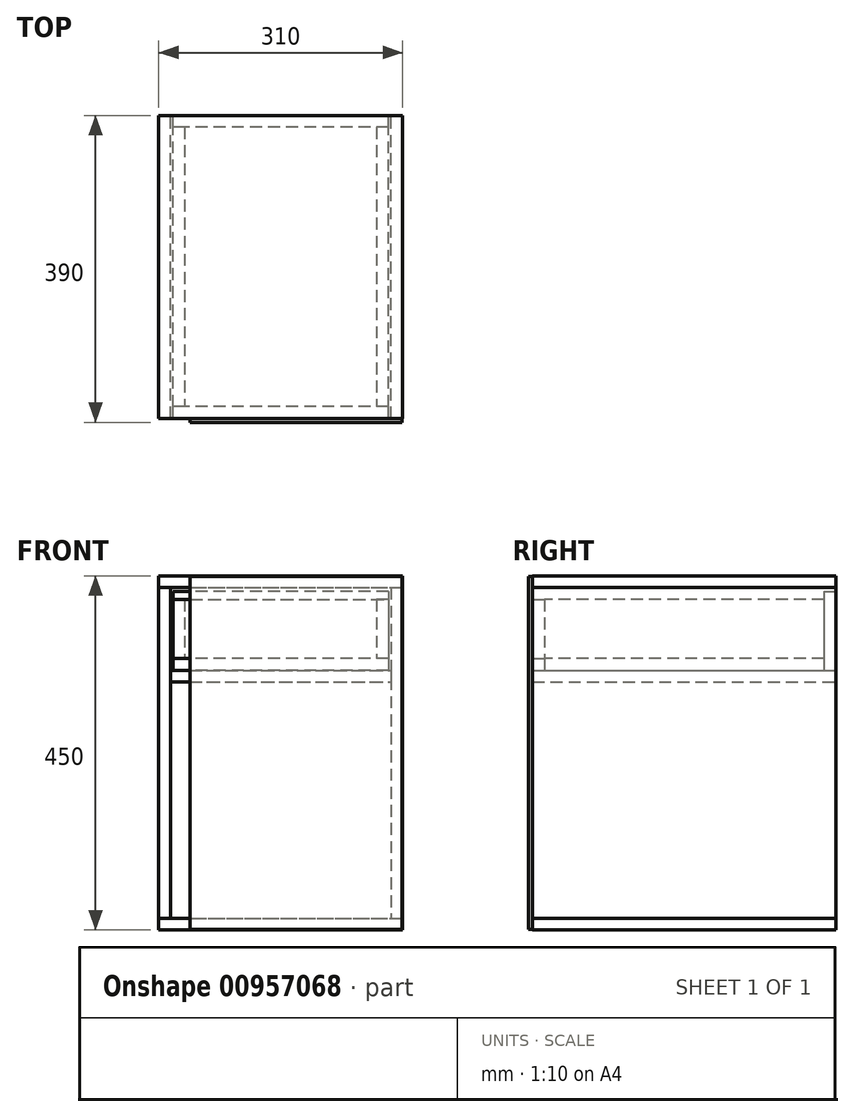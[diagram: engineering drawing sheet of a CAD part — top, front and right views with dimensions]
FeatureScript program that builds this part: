
annotation { "Feature Type Name" : "Feature", "Feature Type Description" : "" }
export const myFeature = defineFeature(function(context is Context, id is Id, definition is map)
    precondition{}
    {
        {
            var Q0;
            Q0=qCreatedBy(makeId("Top.planeOp"),FACE);
            var sketch = newSketch(context, id + "F0", { "sketchPlane" : qUnion([Q0])});
            skLineSegment(sketch, "E0.bottom", {"start": v(0, 0) * mm, "end": v(310, 0) * mm});
            skLineSegment(sketch, "E0.top", {"start": v(0, 385) * mm, "end": v(310, 385) * mm});
            skLineSegment(sketch, "E0.left", {"start": v(0, 0) * mm, "end": v(0, 385) * mm});
            skLineSegment(sketch, "E0.right", {"start": v(310, 0) * mm, "end": v(310, 385) * mm});
            skSolve(sketch);
        }
        {
            var Q0;
            Q0 = qSketchRegion(id + "F0", true);
            extrude(context, id + "F1", {"entities" : qUnion([Q0]), "depth" : 15 * mm, "offsetDistance" : 25 * mm});
        }
        {
            var Q0;
            Q0=makeQuery(id+"F1.opExtrude","CAP_FACE",FACE,{"disambiguationData":[OSD([sQuery(id+"F0.wireOp",EDGE,"E0.bottom"),sQuery(id+"F0.wireOp",EDGE,"E0.top"),sQuery(id+"F0.wireOp",EDGE,"E0.left"),sQuery(id+"F0.wireOp",EDGE,"E0.right")])],"isStart":false});
            var sketch = newSketch(context, id + "F2", { "sketchPlane" : qUnion([Q0])});
            skLineSegment(sketch, "E1.bottom", {"start": v(0, 0) * mm, "end": v(15, 0) * mm});
            skLineSegment(sketch, "E1.top", {"start": v(0, 385) * mm, "end": v(15, 385) * mm});
            skLineSegment(sketch, "E1.left", {"start": v(0, 0) * mm, "end": v(0, 385) * mm});
            skLineSegment(sketch, "E1.right", {"start": v(15, 0) * mm, "end": v(15, 385) * mm});
            skLineSegment(sketch, "E2.bottom", {"start": v(310, 0) * mm, "end": v(295, 0) * mm});
            skLineSegment(sketch, "E2.top", {"start": v(310, 385) * mm, "end": v(295, 385) * mm});
            skLineSegment(sketch, "E2.left", {"start": v(310, 0) * mm, "end": v(310, 385) * mm});
            skLineSegment(sketch, "E2.right", {"start": v(295, 0) * mm, "end": v(295, 385) * mm});
            skSolve(sketch);
        }
        {
            var Q0;
            Q0 = qSketchRegion(id + "F2", true);
            extrude(context, id + "F3", {"entities" : qUnion([Q0]), "depth" : (300 + 15 + 100 + 5) * mm, "offsetDistance" : 25 * mm});
        }
        {
            var Q0;
            Q0=makeQuery(id+"F1.opExtrude","CAP_FACE",FACE,{"disambiguationData":[OSD([sQuery(id+"F0.wireOp",EDGE,"E0.bottom"),sQuery(id+"F0.wireOp",EDGE,"E0.top"),sQuery(id+"F0.wireOp",EDGE,"E0.left"),sQuery(id+"F0.wireOp",EDGE,"E0.right")])],"isStart":false});
            cPlane(context, id + "F4", {"entities" : qUnion([Q0]), "cplaneType" : CPlaneType.OFFSET, "offset" : 300 * mm, "width" : 150 * mm, "height" : 150 * mm});
        }
        {
            var Q0;
            Q0=qCreatedBy(id+"F4.planeOp",FACE);
            var sketch = newSketch(context, id + "F5", { "sketchPlane" : qUnion([Q0])});
            skLineSegment(sketch, "E3.bottom", {"start": v(15, 0) * mm, "end": v(295, 0) * mm});
            skLineSegment(sketch, "E3.top", {"start": v(15, 385) * mm, "end": v(295, 385) * mm});
            skLineSegment(sketch, "E3.left", {"start": v(15, 0) * mm, "end": v(15, 385) * mm});
            skLineSegment(sketch, "E3.right", {"start": v(295, 0) * mm, "end": v(295, 385) * mm});
            skSolve(sketch);
        }
        {
            var Q0;
            Q0 = qSketchRegion(id + "F5", true);
            extrude(context, id + "F6", {"entities" : qUnion([Q0]), "depth" : 15 * mm, "offsetDistance" : 25 * mm});
        }
        {
            var Q0;
            Q0=makeQuery(id+"F3.opExtrude","CAP_FACE",FACE,{"disambiguationData":[OSD([sQuery(id+"F2.wireOp",EDGE,"E1.bottom"),sQuery(id+"F2.wireOp",EDGE,"E1.top"),sQuery(id+"F2.wireOp",EDGE,"E1.left"),sQuery(id+"F2.wireOp",EDGE,"E1.right")])],"isStart":false});
            var sketch = newSketch(context, id + "F7", { "sketchPlane" : qUnion([Q0])});
            skLineSegment(sketch, "E4.bottom", {"start": v(0, 0) * mm, "end": v(310, 0) * mm});
            skLineSegment(sketch, "E4.top", {"start": v(0, 385) * mm, "end": v(310, 385) * mm});
            skLineSegment(sketch, "E4.left", {"start": v(0, 0) * mm, "end": v(0, 385) * mm});
            skLineSegment(sketch, "E4.right", {"start": v(310, 0) * mm, "end": v(310, 385) * mm});
            skSolve(sketch);
        }
        {
            var Q0;
            Q0 = qSketchRegion(id + "F7", true);
            extrude(context, id + "F8", {"entities" : qUnion([Q0]), "depth" : 15 * mm, "offsetDistance" : 25 * mm});
        }
        {
            var Q0;
            Q0=makeQuery(id+"F3.opExtrude","SWEPT_FACE",FACE,{"disambiguationData":[OSD([sQuery(id+"F2.wireOp",EDGE,"E2.bottom")])]});
            var sketch = newSketch(context, id + "F9", { "sketchPlane" : qUnion([Q0])});
            skLineSegment(sketch, "E5.bottom", {"start": v(309, 1) * mm, "end": v(40, 1) * mm});
            skLineSegment(sketch, "E5.top", {"start": v(309, 449) * mm, "end": v(40, 449) * mm});
            skLineSegment(sketch, "E5.left", {"start": v(309, 1) * mm, "end": v(309, 449) * mm});
            skLineSegment(sketch, "E5.right", {"start": v(40, 1) * mm, "end": v(40, 449) * mm});
            skSolve(sketch);
        }
        {
            var Q0;
            Q0 = qSketchRegion(id + "F9", true);
            extrude(context, id + "F10", {"entities" : qUnion([Q0]), "depth" : 5 * mm, "offsetDistance" : 25 * mm});
        }
        {
            var Q0;
            Q0=makeQuery(id+"F3.opExtrude","SWEPT_FACE",FACE,{"disambiguationData":[OSD([sQuery(id+"F2.wireOp",EDGE,"E2.top")])]});
            var sketch = newSketch(context, id + "F11", { "sketchPlane" : qUnion([Q0])});
            skLineSegment(sketch, "E6.bottom", {"start": v(-292, 430) * mm, "end": v(-18, 430) * mm});
            skLineSegment(sketch, "E6.top", {"start": v(-292, 330) * mm, "end": v(-18, 330) * mm});
            skLineSegment(sketch, "E6.left", {"start": v(-292, 430) * mm, "end": v(-292, 330) * mm});
            skLineSegment(sketch, "E6.right", {"start": v(-18, 430) * mm, "end": v(-18, 330) * mm});
            skSolve(sketch);
        }
        {
            var Q0;
            Q0=makeQuery(id+"F11.imprint","IMPRINT",FACE,{"disambiguationData":[TD([[makeQuery(id+"F11.imprint","IMPRINT",EDGE,{"derivedFrom":sQuery(id+"F11.wireOp",EDGE,"E6.bottom")}),-1.0]])]});
            extrude(context, id + "F12", {"entities" : qUnion([Q0]), "oppositeDirection" : true, "depth" : 15 * mm, "offsetDistance" : 25 * mm});
        }
        {
            var Q0;
            Q0=makeQuery(id+"F12.opExtrude","CAP_FACE",FACE,{"disambiguationData":[OSD([sQuery(id+"F11.wireOp",EDGE,"E6.bottom"),sQuery(id+"F11.wireOp",EDGE,"E6.top"),sQuery(id+"F11.wireOp",EDGE,"E6.left"),sQuery(id+"F11.wireOp",EDGE,"E6.right")])],"isStart":false});
            var sketch = newSketch(context, id + "F13", { "sketchPlane" : qUnion([Q0])});
            skLineSegment(sketch, "E7.bottom", {"start": v(292, 330) * mm, "end": v(18, 330) * mm});
            skLineSegment(sketch, "E7.top", {"start": v(292, 345) * mm, "end": v(18, 345) * mm});
            skLineSegment(sketch, "E7.left", {"start": v(292, 330) * mm, "end": v(292, 345) * mm});
            skLineSegment(sketch, "E7.right", {"start": v(18, 330) * mm, "end": v(18, 345) * mm});
            skSolve(sketch);
        }
        {
            var Q0;
            Q0 = qSketchRegion(id + "F13", true);
            extrude(context, id + "F14", {"entities" : qUnion([Q0]), "depth" : (385 - 15 - 15) * mm, "offsetDistance" : 25 * mm});
        }
        {
            var Q0;
            Q0=makeQuery(id+"F14.opExtrude","CAP_FACE",FACE,{"disambiguationData":[OSD([sQuery(id+"F13.wireOp",EDGE,"E7.bottom"),sQuery(id+"F13.wireOp",EDGE,"E7.top"),sQuery(id+"F13.wireOp",EDGE,"E7.left"),sQuery(id+"F13.wireOp",EDGE,"E7.right")])],"isStart":false});
            var sketch = newSketch(context, id + "F15", { "sketchPlane" : qUnion([Q0])});
            skLineSegment(sketch, "E8.bottom", {"start": v(18, 345) * mm, "end": v(292, 345) * mm});
            skLineSegment(sketch, "E8.top", {"start": v(18, 420) * mm, "end": v(292, 420) * mm});
            skLineSegment(sketch, "E8.left", {"start": v(18, 345) * mm, "end": v(18, 420) * mm});
            skLineSegment(sketch, "E8.right", {"start": v(292, 345) * mm, "end": v(292, 420) * mm});
            skSolve(sketch);
        }
        {
            var Q0;
            Q0 = qSketchRegion(id + "F15", true);
            extrude(context, id + "F16", {"entities" : qUnion([Q0]), "depth" : 15 * mm, "offsetDistance" : 25 * mm});
        }
        {
            var Q0;
            Q0=makeQuery(id+"F14.opExtrude","SWEPT_FACE",FACE,{"disambiguationData":[OSD([sQuery(id+"F13.wireOp",EDGE,"E7.top")])]});
            var sketch = newSketch(context, id + "F17", { "sketchPlane" : qUnion([Q0])});
            skLineSegment(sketch, "E9.bottom", {"start": v(18, 370) * mm, "end": v(33, 370) * mm});
            skLineSegment(sketch, "E9.top", {"start": v(18, 15) * mm, "end": v(33, 15) * mm});
            skLineSegment(sketch, "E9.left", {"start": v(18, 370) * mm, "end": v(18, 15) * mm});
            skLineSegment(sketch, "E9.right", {"start": v(33, 370) * mm, "end": v(33, 15) * mm});
            skLineSegment(sketch, "E10.bottom", {"start": v(292, 370) * mm, "end": v(277, 370) * mm});
            skLineSegment(sketch, "E10.top", {"start": v(292, 15) * mm, "end": v(277, 15) * mm});
            skLineSegment(sketch, "E10.left", {"start": v(292, 370) * mm, "end": v(292, 15) * mm});
            skLineSegment(sketch, "E10.right", {"start": v(277, 370) * mm, "end": v(277, 15) * mm});
            skSolve(sketch);
        }
        {
            var Q0;
            Q0 = qSketchRegion(id + "F17", true);
            extrude(context, id + "F18", {"entities" : qUnion([Q0]), "depth" : 75 * mm, "offsetDistance" : 25 * mm});
        }
    });
